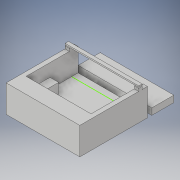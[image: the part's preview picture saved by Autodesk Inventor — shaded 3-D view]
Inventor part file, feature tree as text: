
AUTODESK INVENTOR PART (.ipt)
format: ipt  version: 2019 (Build 230136000, 136)  size: 204,288 bytes
history: native  units: mm
features: sketch x9, extrude x8
ambient origin geometry x8: Origin, YZ Plane, XZ Plane, XY Plane, X Axis, Y Axis, Z Axis, Center Point
bodies: Solid1 (feature_tree)
feature tree (17):
  extrude  "Extrusion1"  Depth=1460.0mm
  extrude  "Extrusion2"  Depth=200.0mm
  extrude  "Extrusion3"  Depth=200.0mm
  extrude  "Extrusion4"  Depth=235.0mm TaperAngle=0.0deg
  extrude  "Extrusion5"  Depth=100.0mm
  extrude  "Extrusion6"  Depth=100.0mm
  extrude  "Extrusion7"  Depth=260.0mm
  extrude  "Extrusion8"  Depth=1500.0mm TaperAngle=0.0deg
  sketch  "Sketch9"  dims[d20=120.0mm d21=120.0mm d22=80.0mm d23=80.0mm d24=110.0mm d25=0.0mm d26=30.0mm d27=1700.0mm d28=20.0mm d29=80.0mm d30=0.0mm d31=80.0mm d32=30.0mm d33=1500.0mm d34=0.0mm d35=100.0mm d36=0.0mm d37=50.0mm d38=90.0deg d39=510.0mm d40=90.0deg d41=510.0mm d42=100.0mm d43=1700.0mm d44=0.0mm]
  sketch  "Sketch1"  dims[d0=1500.0mm d1=1460.0mm]
  sketch  "Sketch2"  dims[d2=100.0mm d3=0.0mm d4=200.0mm]
  sketch  "Sketch3"  dims[d5=810.0mm d6=200.0mm]
  sketch  "Sketch4"  dims[d7=810.0mm d8=235.0mm d9=0.0mm]
  sketch  "Sketch5"  dims[d10=100.0mm d11=100.0mm]
  sketch  "Sketch6"  dims[d12=1700.0mm d13=100.0mm]
  sketch  "Sketch7"  dims[d14=630.0mm d15=0.0mm d16=260.0mm]
  sketch  "Sketch8"  dims[d17=60.0mm d18=1500.0mm d19=0.0mm]
